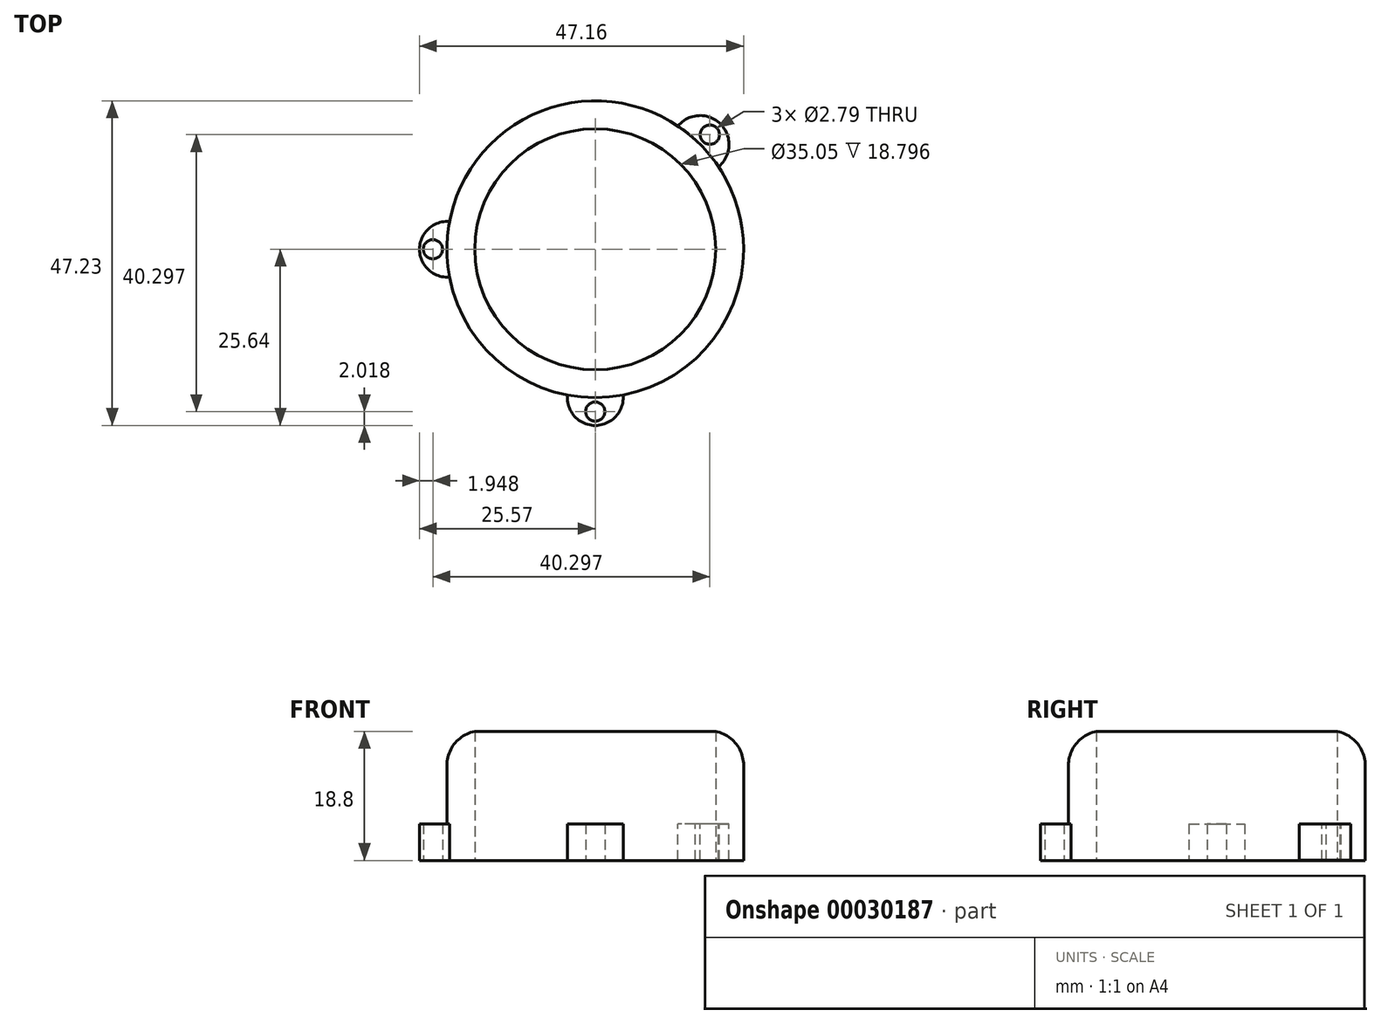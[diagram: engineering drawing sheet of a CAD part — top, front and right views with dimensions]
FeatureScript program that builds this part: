
annotation { "Feature Type Name" : "Feature", "Feature Type Description" : "" }
export const myFeature = defineFeature(function(context is Context, id is Id, definition is map)
    precondition{}
    {
        {
            var Q0;
            Q0=qCreatedBy(makeId("Top.planeOp"),FACE);
            var sketch = newSketch(context, id + "F0", { "sketchPlane" : qUnion([Q0])});
            skCircle(sketch, "E0", {"center": v(0, 0) * mm, "radius": 21.59 * mm});
            skCircle(sketch, "E1", {"center": v(0, 0) * mm, "radius": 17.53 * mm});
            skCircle(sketch, "E2", {"center": v(0, 0) * mm, "radius": 14.03 * mm});
            skSolve(sketch);
        }
        {
            var Q0;
            Q0 = qSketchRegion(id + "F0", true);
            extrude(context, id + "F1", {"entities" : qUnion([Q0]), "depth" : 18.8 * mm});
        }
        {
            var Q0;
            {var subQ0=sQuery(id+"F0.wireOp",EDGE,"E1");Q0=makeQuery(id+"FP3RAwdQIMNU6N7_1.boolean.opBoolean","MERGE",FACE,{"derivedFrom":[makeQuery(id+"F1.opExtrude","CAP_FACE",FACE,{"disambiguationData":[OSD([sQuery(id+"F0.wireOp",EDGE,"E0"),subQ0,sQuery(id+"F0.wireOp",EDGE,"33e30457-8ff7-40ea-9cad-831cd24ae717"),sQuery(id+"F0.wireOp",EDGE,"34f7aef0-b970-4f55-8119-1e8253cd00c9"),sQuery(id+"F0.wireOp",EDGE,"131609cf-2ce5-4336-be42-4ddd0e56d86c"),sQuery(id+"F0.wireOp",EDGE,"87156f82-ffd8-467a-b7e8-e21eb25bcf6a")])],"isStart":true}),makeQuery(id+"FP3RAwdQIMNU6N7_1.opExtrude","CAP_FACE",FACE,{"disambiguationData":[OSD([subQ0,sQuery(id+"F0.wireOp",EDGE,"E2")])],"isStart":true})]});}
            var sketch = newSketch(context, id + "F2", { "sketchPlane" : qUnion([Q0])});
            skCircle(sketch, "E3", {"center": v(-23.62, 0) * mm, "radius": 1.4 * mm});
            skCircle(sketch, "E4", {"center": v(0, 23.62) * mm, "radius": 1.4 * mm});
            skPoint(sketch, "E5.center.orphan", {"position": v(0, 21.59) * mm});
            skArc(sketch, "E6", {"start": v(4.05, 21.2) * mm, "mid": v(0, 25.64) * mm, "end": v(-4.05, 21.2) * mm});
            skArc(sketch, "E7", {"start": v(-21.2, 4.05) * mm, "mid": v(-25.57, 0) * mm, "end": v(-21.2, -4.05) * mm});
            skArc(sketch, "E8", {"start": v(4.05, 21.2) * mm, "mid": v(0, 21.59) * mm, "end": v(-4.05, 21.2) * mm});
            skArc(sketch, "E9", {"start": v(-21.2, 4.05) * mm, "mid": v(-21.5, 0) * mm, "end": v(-21.2, -4.05) * mm});
            skLineSegment(sketch, "E10", {"start": v(-23.62, 0) * mm, "end": v(-21.59, 0) * mm, "construction": true});
            skArc(sketch, "E11", {"start": v(-21.2, 4.05) * mm, "mid": v(-26.44, 0) * mm, "end": v(-21.2, -4.05) * mm});
            skArc(sketch, "E12", {"start": v(4.05, 21.2) * mm, "mid": v(0, 26.37) * mm, "end": v(-4.05, 21.2) * mm});
            skSolve(sketch);
        }
        {
            var Q0;
            Q0=makeQuery(id+"F2.imprint","IMPRINT",FACE,{"disambiguationData":[TD([[makeQuery(id+"F2.imprint","IMPRINT",EDGE,{"derivedFrom":sQuery(id+"F2.wireOp",EDGE,"E3")}),-1.0]])]});
            var Q1;
            {var subQ2=sQuery(id+"F2.wireOp",EDGE,"E9");Q1=makeQuery(id+"F2.imprint","IMPRINT",FACE,{"disambiguationData":[TD([[makeQuery(id+"F2.imprint","IMPRINT",EDGE,{"derivedFrom":subQ2}),-1.0]])]});}
            var Q2;
            Q2=makeQuery(id+"F2.imprint","IMPRINT",FACE,{"disambiguationData":[TD([[makeQuery(id+"F2.imprint","IMPRINT",EDGE,{"derivedFrom":sQuery(id+"F2.wireOp",EDGE,"E4")}),-1.0]])]});
            extrude(context, id + "F3", {"entities" : qUnion([Q0, Q1, Q2]), "operationType" : NewBodyOperationType.ADD, "oppositeDirection" : true, "depth" : 5.33 * mm});
        }
        {
            var Q0;
            Q0=makeQuery(id+"F3.opExtrude","CAP_FACE",FACE,{"disambiguationData":[OSD([sQuery(id+"F2.wireOp",EDGE,"E3"),sQuery(id+"F2.wireOp",EDGE,"E7"),sQuery(id+"F2.wireOp",EDGE,"E9")])],"isStart":false});
            var sketch = newSketch(context, id + "F4", { "sketchPlane" : qUnion([Q0])});
            skArc(sketch, "E13", {"start": v(17.91, 12) * mm, "mid": v(18.25, 18.2) * mm, "end": v(12.03, 17.95) * mm});
            skCircle(sketch, "E14", {"center": v(16.68, 16.68) * mm, "radius": 1.4 * mm});
            skArc(sketch, "E15", {"start": v(17.91, 12) * mm, "mid": v(15.26, 15.26) * mm, "end": v(12.03, 17.95) * mm});
            skLineSegment(sketch, "E16", {"start": v(0, 0) * mm, "end": v(21.9, 21.9) * mm});
            skSolve(sketch);
        }
        {
            var Q0;
            Q0=makeQuery(id+"F4.imprint","IMPRINT",FACE,{"disambiguationData":[TD([[makeQuery(id+"F4.imprint","IMPRINT",EDGE,{"derivedFrom":sQuery(id+"F4.wireOp",EDGE,"E13")}),1.0]])]});
            extrude(context, id + "F5", {"entities" : qUnion([Q0]), "operationType" : NewBodyOperationType.ADD, "oppositeDirection" : true, "depth" : 5.32 * mm});
        }
        {
            var Q0;
            Q0=makeQuery(id+"F1.opExtrude","CAP_EDGE",EDGE,{"disambiguationData":[OSD([sQuery(id+"F0.wireOp",EDGE,"E0")])],"isStart":false});
            fillet(context, id + "F6", {"entities" : qUnion([Q0]), "radius" : 5.08 * mm, "tangentPropagation" : true, "allowEdgeOverflow" : false});
        }
    });
